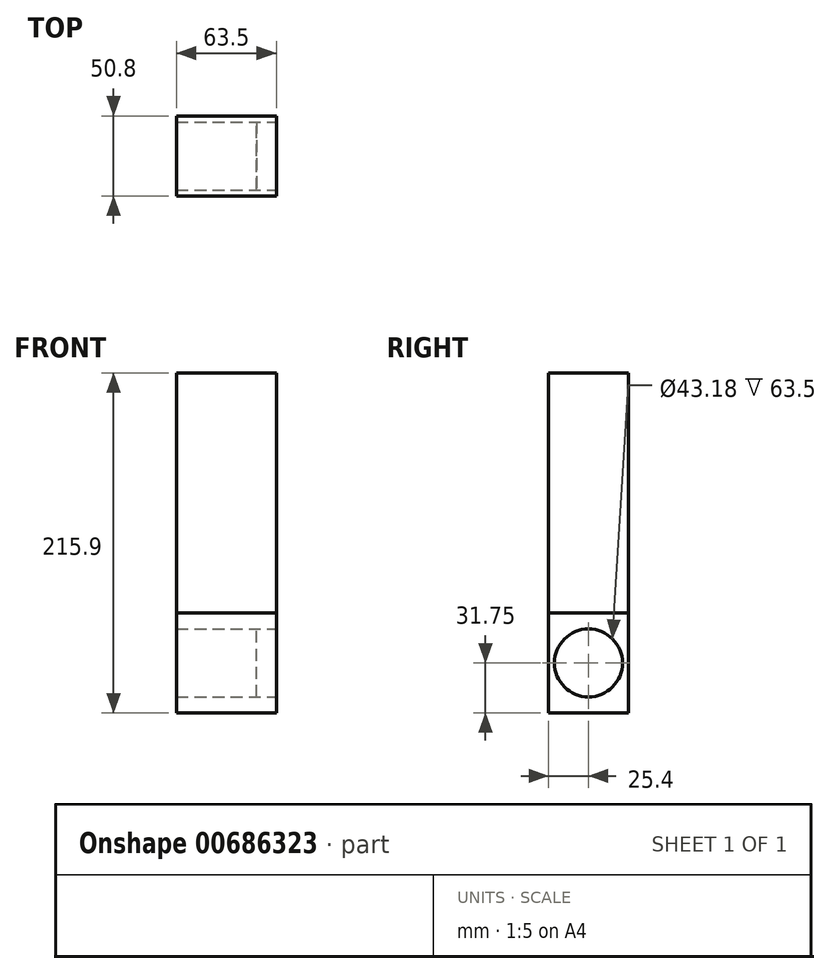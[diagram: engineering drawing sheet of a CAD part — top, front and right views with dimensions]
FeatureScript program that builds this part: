
annotation { "Feature Type Name" : "Feature", "Feature Type Description" : "" }
export const myFeature = defineFeature(function(context is Context, id is Id, definition is map)
    precondition{}
    {
        {
            var Q0;
            Q0=qCreatedBy(makeId("Right.planeOp"),FACE);
            var sketch = newSketch(context, id + "F0", { "sketchPlane" : qUnion([Q0])});
            skLineSegment(sketch, "E0.bottom", {"start": v(-25.4, 76.2) * mm, "end": v(25.4, 76.2) * mm});
            skLineSegment(sketch, "E0.top", {"start": v(-25.4, -76.2) * mm, "end": v(25.4, -76.2) * mm});
            skLineSegment(sketch, "E0.left", {"start": v(-25.4, 76.2) * mm, "end": v(-25.4, -76.2) * mm});
            skLineSegment(sketch, "E0.right", {"start": v(25.4, 76.2) * mm, "end": v(25.4, -76.2) * mm});
            skPoint(sketch, "E0.middle", {"position": v(0, 0) * mm});
            skSolve(sketch);
        }
        {
            var Q0;
            Q0=makeQuery(id+"F0.imprint","IMPRINT",FACE,{"disambiguationData":[TD([[makeQuery(id+"F0.imprint","IMPRINT",EDGE,{"derivedFrom":sQuery(id+"F0.wireOp",EDGE,"E0.bottom")}),-1.0]])]});
            extrude(context, id + "F1", {"entities" : qUnion([Q0]), "endBound" : BoundingType.SYMMETRIC, "depth" : 63.5 * mm, "offsetDistance" : 25.4 * mm});
        }
        {
            var Q0;
            Q0=makeQuery(id+"F1.opExtrude","CAP_FACE",FACE,{"disambiguationData":[OSD([sQuery(id+"F0.wireOp",EDGE,"E0.bottom"),sQuery(id+"F0.wireOp",EDGE,"E0.top"),sQuery(id+"F0.wireOp",EDGE,"E0.left"),sQuery(id+"F0.wireOp",EDGE,"E0.right")])],"isStart":false});
            var sketch = newSketch(context, id + "F2", { "sketchPlane" : qUnion([Q0])});
            skLineSegment(sketch, "E1.bottom", {"start": v(-25.4, -76.2) * mm, "end": v(25.4, -76.2) * mm});
            skLineSegment(sketch, "E1.top", {"start": v(-25.4, -139.7) * mm, "end": v(25.4, -139.7) * mm});
            skLineSegment(sketch, "E1.left", {"start": v(-25.4, -76.2) * mm, "end": v(-25.4, -139.7) * mm});
            skLineSegment(sketch, "E1.right", {"start": v(25.4, -76.2) * mm, "end": v(25.4, -139.7) * mm});
            skCircle(sketch, "E2", {"center": v(0, -107.95) * mm, "radius": 21.59 * mm});
            skPoint(sketch, "E2.centerSnap0", {"position": v(-25.4, -107.95) * mm});
            skSolve(sketch);
        }
        {
            var Q0;
            Q0=makeQuery(id+"F2.imprint","IMPRINT",FACE,{"disambiguationData":[TD([[makeQuery(id+"F2.imprint","IMPRINT",EDGE,{"derivedFrom":sQuery(id+"F2.wireOp",EDGE,"E1.bottom")}),-1.0]])]});
            extrude(context, id + "F3", {"entities" : qUnion([Q0]), "oppositeDirection" : true, "depth" : 63.5 * mm, "offsetDistance" : 25.4 * mm});
        }
        {
            var Q0;
            Q0=makeQuery(id+"F3.opExtrude","CAP_FACE",FACE,{"disambiguationData":[OSD([sQuery(id+"F2.wireOp",EDGE,"E1.bottom"),sQuery(id+"F2.wireOp",EDGE,"E1.top"),sQuery(id+"F2.wireOp",EDGE,"E1.left"),sQuery(id+"F2.wireOp",EDGE,"E1.right"),sQuery(id+"F2.wireOp",EDGE,"E2")])],"isStart":true});
            var sketch = newSketch(context, id + "F4", { "sketchPlane" : qUnion([Q0])});
            skCircle(sketch, "E3", {"center": v(0, -107.95) * mm, "radius": 21.59 * mm});
            skSolve(sketch);
        }
        {
            var Q0;
            Q0=makeQuery(id+"F4.imprint","IMPRINT",FACE,{"disambiguationData":[TD([[makeQuery(id+"F4.imprint","IMPRINT",EDGE,{"derivedFrom":sQuery(id+"F4.wireOp",EDGE,"E3")}),1.0]])]});
            extrude(context, id + "F5", {"entities" : qUnion([Q0]), "oppositeDirection" : true, "depth" : 63.5 * mm, "offsetDistance" : 25.4 * mm, "hasSecondDirection" : true, "secondDirectionOppositeDirection" : true, "secondDirectionDepth" : 12.7 * mm});
        }
    });
